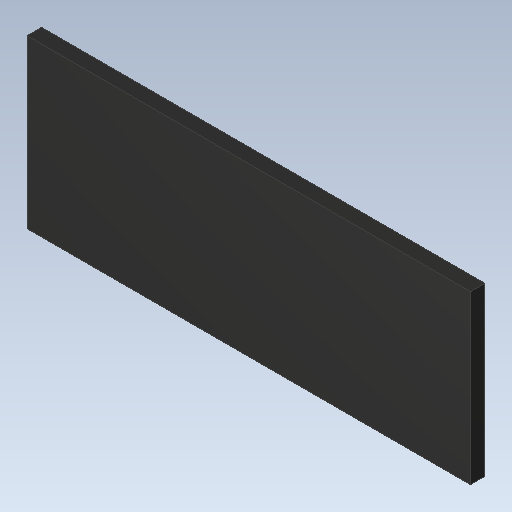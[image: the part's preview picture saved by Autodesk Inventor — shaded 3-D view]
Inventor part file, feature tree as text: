
AUTODESK INVENTOR PART (.ipt)
format: ipt  version: 2020 (Build 240168000, 168)  size: 86,528 bytes
history: imported  units: in
note: dims shown in document units (in); Inventor stores cm internally (conversion verified against a paired STEP export)
features: imported_body x1
ambient origin geometry x8: Origin, YZ Plane, XZ Plane, XY Plane, X Axis, Y Axis, Z Axis, Center Point
bodies: Solid1 (imported_parasolid), Body1 (imported_parasolid)
feature tree (1):
  imported_body  NMx_Import_Brep_tag  [imported B-rep: ~6 faces, bbox_mm=[3.0661, 1.1557, 0.1]]
